# Revit family: HL_Сифон с уплотнением_HL136.2
name_source: partatom
category: Příslušenství trubek
revit_build: Autodesk Revit 2016 (Build: 20161004_0715(x64)
units: mm (PartAtom-declared; Revit-internal decimal feet)

## family parameters
Kóta kulaté spojky = Použít průměr
Nadpis OmniClass = General Pipework and Ductwork Products
Ořezat dutým tvarem při načtení = Ne
Sdílené = Ne
Typ součásti = Normální
Vždy vertikální = Ano
Založené na pracovní rovině = Ne
Číslo OmniClass = 23.60.30.00

## types (1)
- HL_Сифон с уплотнением_HL136.2
    Cena = 0 $
    EAN = 9003076008223
    Komentáře k typům = Сифон с уплотнением DN40 горизонтальный х DN40 горизонтальный с прозрачными патрубками
    Model = HL136.2
    Popis = Кондиционирование и Вентиляция
    URL = http://www.hutterer-lechner.com
    Výrobce = HL Hutterer & Lechner GmbH
    a = 22 mm  [stored 0.0721785 ft]
    ВЕС = 0,364 kg
    МАТЕРИАЛ = PP
    НОМИНАЛЬНЫЙ ДИАМЕТР = 40 mm
    НОМИНАЛЬНЫЙ ДИАМЕТР 2 = 20 mm
    ПРИЁМНОЕ ОТВЕРСТИЕ = WG-Anschluss 3/4"
    ПРОИЗВОДИТЕЛЬНОСТЬ = 0,6 l/s
    ПРОПУСКНАЯ СПОСОБНОСТЬ = 0.0 m³/h
    РАЗМЕР = DN40 x 6/4"
    материал = Plactic - White
    материал 2 = Plactic - Transparent

note: [stored X ft] marks values corroborated as IEEE doubles in the binary element streams (Revit-internal decimal feet)
